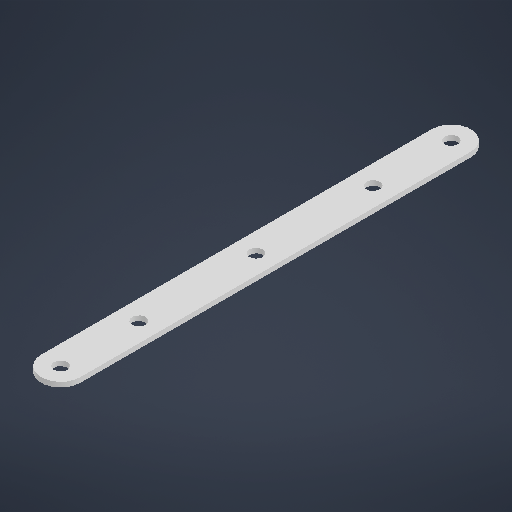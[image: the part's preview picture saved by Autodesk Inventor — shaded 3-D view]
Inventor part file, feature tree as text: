
AUTODESK INVENTOR PART (.ipt)
format: ipt  version: 2025.2 (Build 292293000, 293)  size: 199,168 bytes
history: native  units: in
note: dims shown in document units (in); Inventor stores cm internally (conversion verified against a paired STEP export)
features: extrude x1, sketch x1
ambient origin geometry x8: Origin, YZ Plane, XZ Plane, XY Plane, X Axis, Y Axis, Z Axis, Center Point
bodies: Solid1 (feature_tree)
feature tree (2):
  extrude  "Extrusion1"  Depth=0.0625in
  sketch  "Sketch1"  dims[d0=1.0in d1=1.5in d2=1.5in d3=1.0in d4=0.172in d5=0.172in d6=0.172in d7=0.172in d8=0.5in d9=0.5in d10=0.0625in d11=0.0in d12=0.172in]
